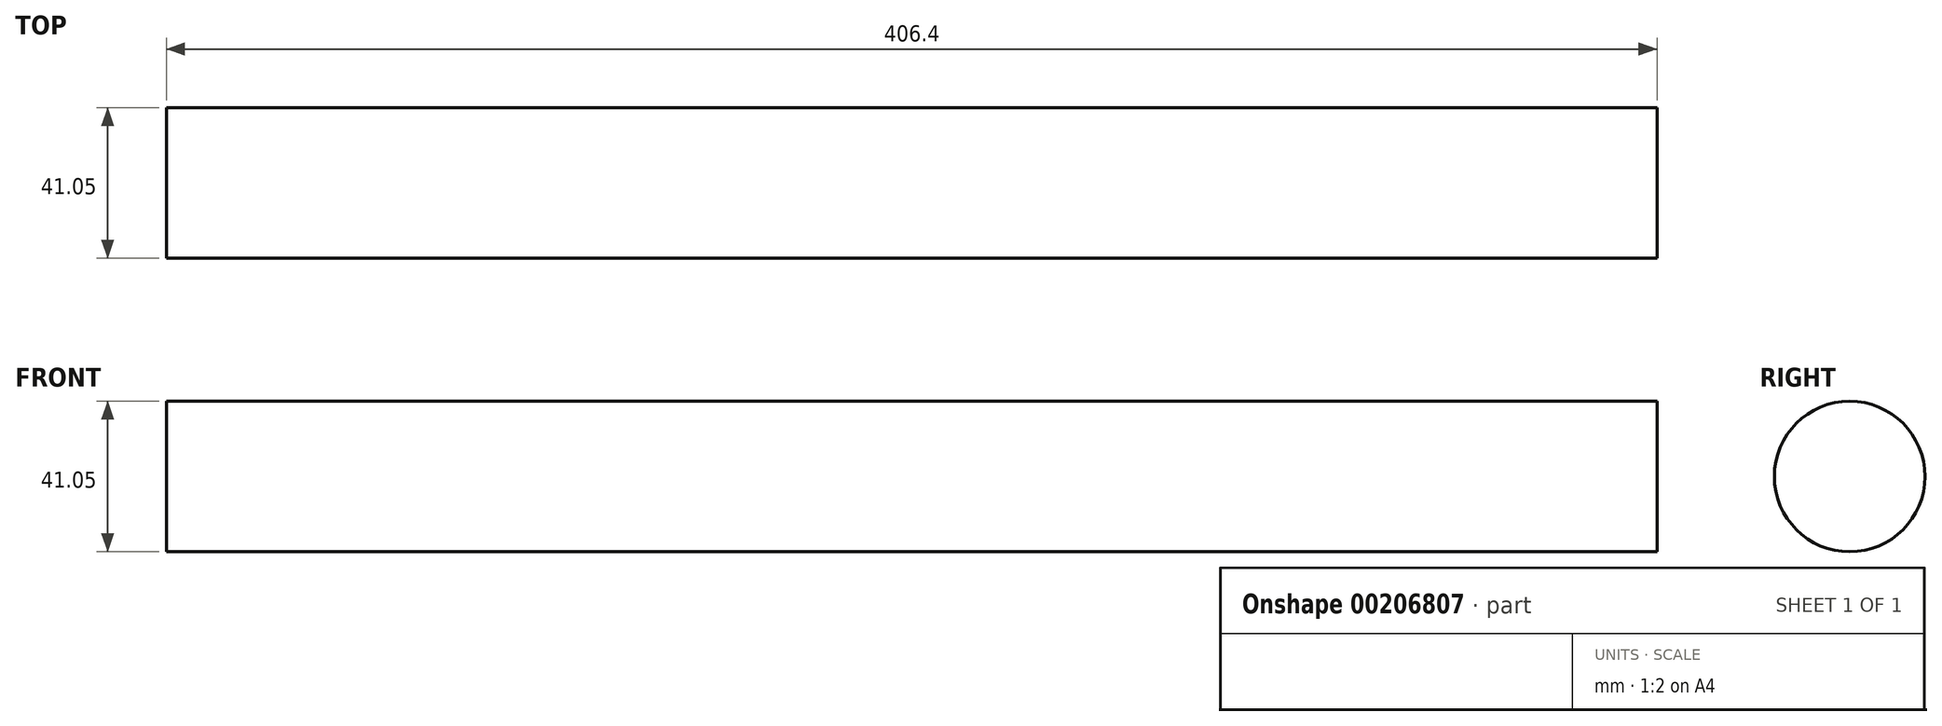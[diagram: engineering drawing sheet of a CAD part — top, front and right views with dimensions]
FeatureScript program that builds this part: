
annotation { "Feature Type Name" : "Feature", "Feature Type Description" : "" }
export const myFeature = defineFeature(function(context is Context, id is Id, definition is map)
    precondition{}
    {
        {
            var Q0;
            Q0=qCreatedBy(makeId("Right.planeOp"),FACE);
            var sketch = newSketch(context, id + "F0", { "sketchPlane" : qUnion([Q0])});
            skCircle(sketch, "E0", {"center": v(-38.14, 16.84) * mm, "radius": 20.52 * mm});
            skSolve(sketch);
        }
        {
            var Q0;
            Q0 = qSketchRegion(id + "F0", true);
            extrude(context, id + "F1", {"entities" : qUnion([Q0]), "endBound" : BoundingType.SYMMETRIC, "depth" : 406.4 * mm});
        }
    });
